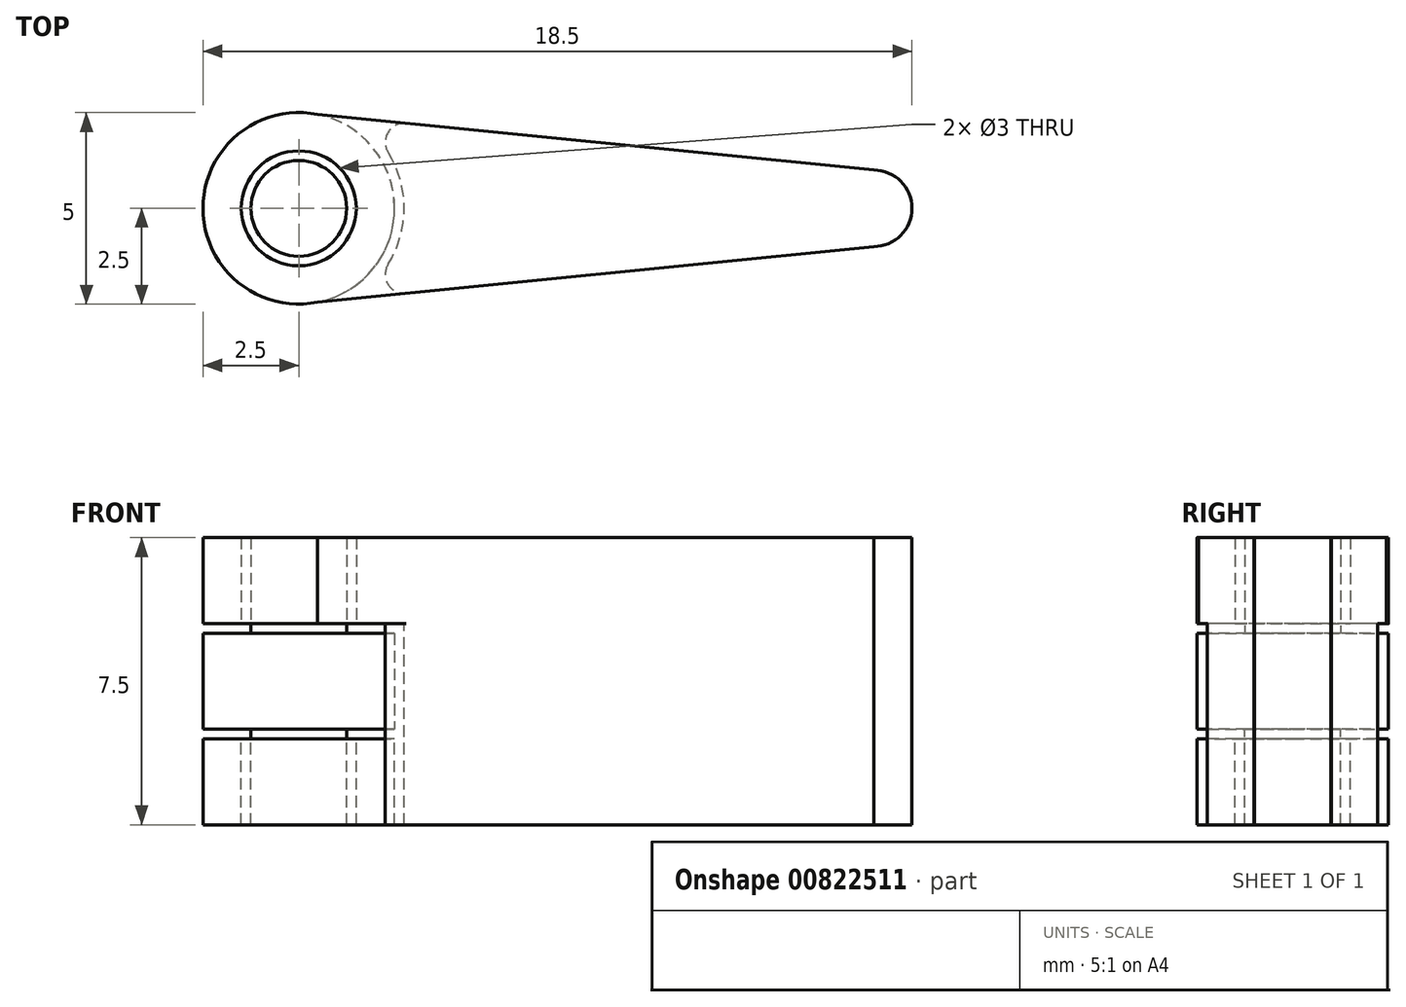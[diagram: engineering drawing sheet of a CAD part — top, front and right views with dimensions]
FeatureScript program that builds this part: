
annotation { "Feature Type Name" : "Feature", "Feature Type Description" : "" }
export const myFeature = defineFeature(function(context is Context, id is Id, definition is map)
    precondition{}
    {
        {
            var Q0;
            Q0=qCreatedBy(makeId("Top.planeOp"),FACE);
            var sketch = newSketch(context, id + "F0", { "sketchPlane" : qUnion([Q0])});
            skCircle(sketch, "E0", {"center": v(0, 0) * mm, "radius": 2.5 * mm});
            skSolve(sketch);
        }
        {
            var Q0;
            Q0 = qSketchRegion(id + "F0", true);
            extrude(context, id + "F1", {"entities" : qUnion([Q0]), "endBound" : BoundingType.SYMMETRIC, "depth" : 2.5 * mm, "offsetDistance" : 25 * mm});
        }
        {
            var Q0;
            Q0=makeQuery(id+"F1.opExtrude","CAP_FACE",FACE,{"disambiguationData":[OSD([sQuery(id+"F0.wireOp",EDGE,"E0")])],"isStart":false});
            var sketch = newSketch(context, id + "F2", { "sketchPlane" : qUnion([Q0])});
            skCircle(sketch, "E1", {"center": v(0, 0) * mm, "radius": 1.25 * mm});
            skSolve(sketch);
        }
        {
            var Q0;
            Q0 = qSketchRegion(id + "F2", true);
            extrude(context, id + "F3", {"entities" : qUnion([Q0]), "operationType" : NewBodyOperationType.ADD, "depth" : 2.5 * mm, "offsetDistance" : 25 * mm});
        }
        {
            var Q0;
            Q0=makeQuery(id+"F1.opExtrude","CAP_FACE",FACE,{"disambiguationData":[OSD([sQuery(id+"F0.wireOp",EDGE,"E0")])],"isStart":true});
            var sketch = newSketch(context, id + "F4", { "sketchPlane" : qUnion([Q0])});
            skCircle(sketch, "E2", {"center": v(0, 0) * mm, "radius": 1.25 * mm});
            skSolve(sketch);
        }
        {
            var Q0;
            Q0 = qSketchRegion(id + "F4", true);
            extrude(context, id + "F5", {"entities" : qUnion([Q0]), "operationType" : NewBodyOperationType.ADD, "depth" : 2.5 * mm, "offsetDistance" : 25 * mm});
        }
        {
            var Q0;
            Q0=makeQuery(id+"F1.opExtrude","CAP_FACE",FACE,{"disambiguationData":[OSD([sQuery(id+"F0.wireOp",EDGE,"E0")])],"isStart":false});
            cPlane(context, id + "F6", {"entities" : qUnion([Q0]), "cplaneType" : CPlaneType.OFFSET, "offset" : 0.25 * mm, "width" : 150 * mm, "height" : 150 * mm});
        }
        {
            var Q0;
            Q0=qCreatedBy(id+"F6.planeOp",FACE);
            var sketch = newSketch(context, id + "F7", { "sketchPlane" : qUnion([Q0])});
            skCircle(sketch, "E3", {"center": v(0, 0) * mm, "radius": 2.5 * mm});
            skCircle(sketch, "E4", {"center": v(0, 0) * mm, "radius": 1.5 * mm});
            skSolve(sketch);
        }
        {
            var Q0;
            Q0=makeQuery(id+"F7.imprint","IMPRINT",FACE,{"disambiguationData":[TD([[makeQuery(id+"F7.imprint","IMPRINT",EDGE,{"derivedFrom":sQuery(id+"F7.wireOp",EDGE,"E3")}),1.0]])]});
            extrude(context, id + "F8", {"entities" : qUnion([Q0]), "depth" : 2.25 * mm, "offsetDistance" : 25 * mm});
        }
        {
            var Q0;
            Q0=makeQuery(id+"F1.opExtrude","CAP_FACE",FACE,{"disambiguationData":[OSD([sQuery(id+"F0.wireOp",EDGE,"E0")])],"isStart":true});
            cPlane(context, id + "F9", {"entities" : qUnion([Q0]), "cplaneType" : CPlaneType.OFFSET, "offset" : 0.25 * mm, "width" : 150 * mm, "height" : 150 * mm});
        }
        {
            var Q0;
            Q0=qCreatedBy(id+"F9.planeOp",FACE);
            var sketch = newSketch(context, id + "F10", { "sketchPlane" : qUnion([Q0])});
            skCircle(sketch, "E5", {"center": v(0, 0) * mm, "radius": 1.5 * mm});
            skCircle(sketch, "E6", {"center": v(0, 0) * mm, "radius": 2.5 * mm});
            skSolve(sketch);
        }
        {
            var Q0;
            Q0=makeQuery(id+"F10.imprint","IMPRINT",FACE,{"disambiguationData":[TD([[makeQuery(id+"F10.imprint","IMPRINT",EDGE,{"derivedFrom":sQuery(id+"F10.wireOp",EDGE,"E5")}),-1.0]])]});
            extrude(context, id + "F11", {"entities" : qUnion([Q0]), "depth" : 2.25 * mm, "offsetDistance" : 25 * mm});
        }
        {
            var Q0;
            Q0=makeQuery(id+"F8.opExtrude","CAP_FACE",FACE,{"disambiguationData":[OSD([sQuery(id+"F7.wireOp",EDGE,"E3"),sQuery(id+"F7.wireOp",EDGE,"E4")])],"isStart":false});
            var sketch = newSketch(context, id + "F12", { "sketchPlane" : qUnion([Q0])});
            skLineSegment(sketch, "E7", {"start": v(0, 0) * mm, "end": v(15, 0) * mm, "construction": true});
            skCircle(sketch, "E8", {"center": v(15, 0) * mm, "radius": 1 * mm});
            skCircle(sketch, "E9", {"center": v(0, 0) * mm, "radius": 2.5 * mm});
            skLineSegment(sketch, "E10", {"start": v(0, 0) * mm, "end": v(0, 2.5) * mm, "construction": true});
            skLineSegment(sketch, "E11", {"start": v(0, 2.5) * mm, "end": v(15, 1) * mm});
            skCircle(sketch, "E12", {"center": v(0, 0) * mm, "radius": 1.5 * mm});
            skLineSegment(sketch, "E13", {"start": v(0, 0) * mm, "end": v(0, -2.5) * mm, "construction": true});
            skLineSegment(sketch, "E14", {"start": v(0, -2.5) * mm, "end": v(15, -1) * mm});
            skLineSegment(sketch, "E15", {"start": v(0, 2.5) * mm, "end": v(0, -2.5) * mm});
            skLineSegment(sketch, "E16", {"start": v(15, -1) * mm, "end": v(15, 1) * mm});
            skSolve(sketch);
        }
        {
            var Q0;
            {var subQ0=sQuery(id+"F12.wireOp",EDGE,"E16");var subQ5=sQuery(id+"F12.wireOp",EDGE,"E8");var subQ6=makeQuery(id+"F12.imprint","INTERSECT",VERTEX,{"disambiguationData":[OD(0.0)],"derivedFrom":[subQ5,subQ0]});Q0=makeQuery(id+"F12.imprint","IMPRINT",FACE,{"disambiguationData":[TD([[makeQuery(id+"F12.imprint","IMPRINT",EDGE,{"disambiguationData":[TD([[subQ6,1.0]])],"derivedFrom":subQ5}),-1.0]])]});}
            var Q1;
            {var subQ4=sQuery(id+"F12.wireOp",EDGE,"E11");var subQ5=sQuery(id+"F12.wireOp",EDGE,"E9");var subQ7=makeQuery(id+"F12.imprint","INTERSECT",VERTEX,{"derivedFrom":[subQ5,subQ4]});Q1=makeQuery(id+"F12.imprint","IMPRINT",FACE,{"disambiguationData":[TD([[makeQuery(id+"F12.imprint","IMPRINT",EDGE,{"disambiguationData":[TD([[subQ7,1.0]])],"derivedFrom":subQ5}),1.0]])]});}
            var Q2;
            {var subQ0=sQuery(id+"F12.wireOp",EDGE,"E15");var subQ4=sQuery(id+"F12.wireOp",EDGE,"E12");var subQ5=makeQuery(id+"F12.imprint","INTERSECT",VERTEX,{"disambiguationData":[OD(0.0)],"derivedFrom":[subQ4,subQ0]});Q2=makeQuery(id+"F12.imprint","IMPRINT",FACE,{"disambiguationData":[TD([[makeQuery(id+"F12.imprint","IMPRINT",EDGE,{"disambiguationData":[TD([[subQ5,-1.0]])],"derivedFrom":subQ4}),-1.0]])]});}
            var Q3;
            {var subQ0=sQuery(id+"F12.wireOp",EDGE,"E16");var subQ1=sQuery(id+"F12.wireOp",EDGE,"E8");var subQ2=makeQuery(id+"F12.imprint","INTERSECT",VERTEX,{"disambiguationData":[OD(0.0)],"derivedFrom":[subQ1,subQ0]});Q3=makeQuery(id+"F12.imprint","IMPRINT",FACE,{"disambiguationData":[TD([[makeQuery(id+"F12.imprint","IMPRINT",EDGE,{"disambiguationData":[TD([[subQ2,-1.0]])],"derivedFrom":subQ1}),1.0]])]});}
            var Q4;
            {var subQ0=sQuery(id+"F12.wireOp",EDGE,"E16");var subQ1=sQuery(id+"F12.wireOp",EDGE,"E8");var subQ2=makeQuery(id+"F12.imprint","INTERSECT",VERTEX,{"disambiguationData":[OD(0.0)],"derivedFrom":[subQ1,subQ0]});Q4=makeQuery(id+"F12.imprint","IMPRINT",FACE,{"disambiguationData":[TD([[makeQuery(id+"F12.imprint","IMPRINT",EDGE,{"disambiguationData":[TD([[subQ2,1.0]])],"derivedFrom":subQ1}),1.0]])]});}
            var Q5;
            Q5=makeQuery(id+"F8.opExtrude","CAP_FACE",FACE,{"disambiguationData":[OSD([sQuery(id+"F7.wireOp",EDGE,"E3"),sQuery(id+"F7.wireOp",EDGE,"E4")])],"isStart":true});
            extrude(context, id + "F13", {"entities" : qUnion([Q0, Q1, Q2, Q3, Q4]), "operationType" : NewBodyOperationType.ADD, "endBound" : BoundingType.UP_TO_SURFACE, "oppositeDirection" : true, "depth" : 25 * mm, "endBoundEntityFace" : qUnion([Q5]), "offsetDistance" : 25 * mm});
        }
        {
            var Q0;
            Q0=makeQuery(id+"F13.boolean.opBoolean","MERGE",FACE,{"derivedFrom":[makeQuery(id+"F8.opExtrude","CAP_FACE",FACE,{"disambiguationData":[OSD([sQuery(id+"F7.wireOp",EDGE,"E3"),sQuery(id+"F7.wireOp",EDGE,"E4")])],"isStart":true}),makeQuery(id+"F13.opExtrude","CAP_FACE",FACE,{"disambiguationData":[OSD([sQuery(id+"F12.wireOp",EDGE,"E8"),sQuery(id+"F12.wireOp",EDGE,"E9"),sQuery(id+"F12.wireOp",EDGE,"E11"),sQuery(id+"F12.wireOp",EDGE,"E12"),sQuery(id+"F12.wireOp",EDGE,"E14"),sQuery(id+"F12.wireOp",EDGE,"E16")])],"isStart":false})]});
            var sketch = newSketch(context, id + "F14", { "sketchPlane" : qUnion([Q0])});
            skLineSegment(sketch, "E17.0", {"start": v(15, 1) * mm, "end": v(0.5, 2.45) * mm});
            skLineSegment(sketch, "E17.1", {"start": v(0.5, -2.45) * mm, "end": v(15, -1) * mm});
            skLineSegment(sketch, "E17.2", {"start": v(15, -1) * mm, "end": v(15, -1) * mm});
            skArc(sketch, "E17.3", {"start": v(0.5, 2.45) * mm, "mid": v(-2.5, 0) * mm, "end": v(0.5, -2.45) * mm});
            skArc(sketch, "E17.4", {"start": v(15, -1) * mm, "mid": v(16, 0) * mm, "end": v(15, 1) * mm});
            skLineSegment(sketch, "E17.5", {"start": v(15, 1) * mm, "end": v(15, 1) * mm});
            skCircle(sketch, "E18.0", {"center": v(0, 0) * mm, "radius": 1.5 * mm});
            skArc(sketch, "E19", {"start": v(1.41, 2.36) * mm, "mid": v(2.75, 0) * mm, "end": v(1.41, -2.36) * mm});
            skLineSegment(sketch, "E20", {"start": v(0, 0) * mm, "end": v(2.75, 0) * mm, "construction": true});
            skSolve(sketch);
        }
        {
            var Q0;
            {var subQ0=sQuery(id+"F14.wireOp",EDGE,"E17.2");Q0=makeQuery(id+"F14.imprint","IMPRINT",FACE,{"disambiguationData":[TD([[makeQuery(id+"F14.imprint","IMPRINT",EDGE,{"derivedFrom":subQ0}),1.0]])]});}
            var Q1;
            Q1=makeQuery(id+"F11.opExtrude","CAP_FACE",FACE,{"disambiguationData":[OSD([sQuery(id+"F10.wireOp",EDGE,"E5"),sQuery(id+"F10.wireOp",EDGE,"E6")])],"isStart":true});
            extrude(context, id + "F15", {"entities" : qUnion([Q0]), "operationType" : NewBodyOperationType.ADD, "endBound" : BoundingType.UP_TO_SURFACE, "depth" : 25 * mm, "endBoundEntityFace" : qUnion([Q1]), "offsetDistance" : 25 * mm});
        }
        {
            var Q0;
            Q0=makeQuery(id+"F11.opExtrude","CAP_FACE",FACE,{"disambiguationData":[OSD([sQuery(id+"F10.wireOp",EDGE,"E5"),sQuery(id+"F10.wireOp",EDGE,"E6")])],"isStart":false});
            var sketch = newSketch(context, id + "F16", { "sketchPlane" : qUnion([Q0])});
            skArc(sketch, "E21.0", {"start": v(15, -1) * mm, "mid": v(16, 0) * mm, "end": v(15, 1) * mm});
            skLineSegment(sketch, "E21.1", {"start": v(15, 1) * mm, "end": v(1.41, 2.36) * mm});
            skArc(sketch, "E21.2", {"start": v(1.41, 2.36) * mm, "mid": v(2.75, 0) * mm, "end": v(1.41, -2.36) * mm});
            skLineSegment(sketch, "E21.3", {"start": v(15, 1) * mm, "end": v(15, 1) * mm});
            skLineSegment(sketch, "E21.4", {"start": v(1.41, -2.36) * mm, "end": v(15, -1) * mm});
            skLineSegment(sketch, "E21.5", {"start": v(15, -1) * mm, "end": v(15, -1) * mm});
            skCircle(sketch, "E22", {"center": v(0, 0) * mm, "radius": 2.5 * mm});
            skCircle(sketch, "E23", {"center": v(0, 0) * mm, "radius": 1.5 * mm});
            skLineSegment(sketch, "E24", {"start": v(1.41, 2.36) * mm, "end": v(0, 2.5) * mm});
            skLineSegment(sketch, "E25", {"start": v(1.41, -2.36) * mm, "end": v(0, -2.5) * mm});
            skLineSegment(sketch, "E26", {"start": v(0, 0) * mm, "end": v(0, 2.5) * mm, "construction": true});
            skLineSegment(sketch, "E27", {"start": v(0, 0) * mm, "end": v(0, -2.5) * mm, "construction": true});
            skSolve(sketch);
        }
        {
            var Q0;
            {var subQ0=sQuery(id+"F16.wireOp",EDGE,"E21.2");Q0=makeQuery(id+"F16.imprint","IMPRINT",FACE,{"disambiguationData":[TD([[makeQuery(id+"F16.imprint","IMPRINT",EDGE,{"derivedFrom":subQ0}),-1.0]])]});}
            var Q1;
            Q1=makeQuery(id+"F16.imprint","IMPRINT",FACE,{"disambiguationData":[TD([[makeQuery(id+"F16.imprint","IMPRINT",EDGE,{"derivedFrom":sQuery(id+"F16.wireOp",EDGE,"E23")}),-1.0]])]});
            var Q2;
            Q2=makeQuery(id+"F16.imprint","IMPRINT",FACE,{"disambiguationData":[TD([[makeQuery(id+"F16.imprint","IMPRINT",EDGE,{"derivedFrom":sQuery(id+"F16.wireOp",EDGE,"E21.0")}),1.0]])]});
            var Q3;
            Q3=makeQuery(id+"F15.opExtrude","CAP_FACE",FACE,{"disambiguationData":[OSD([sQuery(id+"F14.wireOp",EDGE,"E17.0"),sQuery(id+"F14.wireOp",EDGE,"E17.1"),sQuery(id+"F14.wireOp",EDGE,"E17.2"),sQuery(id+"F14.wireOp",EDGE,"E17.4"),sQuery(id+"F14.wireOp",EDGE,"E17.5"),sQuery(id+"F14.wireOp",EDGE,"E19")])],"isStart":false});
            extrude(context, id + "F17", {"entities" : qUnion([Q0, Q1, Q2]), "operationType" : NewBodyOperationType.ADD, "endBound" : BoundingType.UP_TO_SURFACE, "oppositeDirection" : true, "depth" : 25 * mm, "endBoundEntityFace" : qUnion([Q3]), "offsetDistance" : 25 * mm});
        }
        {
            var Q0;
            Q0=makeQuery(id+"F15.opExtrude","SWEPT_EDGE",EDGE,{"disambiguationData":[OSD([sQuery(id+"F14.wireOp",EDGE,"E17.1"),sQuery(id+"F14.wireOp",EDGE,"E19")])]});
            var Q1;
            Q1=makeQuery(id+"F15.opExtrude","SWEPT_EDGE",EDGE,{"disambiguationData":[OSD([sQuery(id+"F14.wireOp",EDGE,"E17.0"),sQuery(id+"F14.wireOp",EDGE,"E19")])]});
            fillet(context, id + "F18", {"entities" : qUnion([Q0, Q1]), "radius" : 0.5 * mm, "tangentPropagation" : true, "allowEdgeOverflow" : false});
        }
    });
